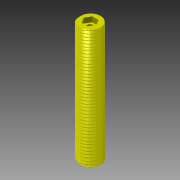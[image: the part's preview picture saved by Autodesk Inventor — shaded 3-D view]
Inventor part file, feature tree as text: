
AUTODESK INVENTOR PART (.ipt)
format: ipt  version: 2013 (Build 170138000, 138)  size: 762,880 bytes
history: native  units: mm
features: sketch x3, extrude x2, helix x1, projected_geometry x1
ambient origin geometry x8: Origin, YZ Plane, XZ Plane, XY Plane, X Axis, Y Axis, Z Axis, Center Point
bodies: Solid1 (feature_tree)
feature tree (7):
  extrude  "Extrusion1"  Depth=5.0mm
  helix  "Coil1"  [1 undecoded]
  extrude  "Extrusion2"  Depth=7.5mm
  sketch  "Sketch1"  dims[d0=14.8mm d2=5.0mm d3=82.0mm d4=0.0mm]
  sketch  "Sketch2"  dims[d5=2.0mm]
  sketch  "Sketch3"  dims[d6=2.001mm d7=10.0mm d8=500.0mm d9=0.0mm d10=90.0deg d11=90.0deg d12=0.0mm d13=0.0mm d14=7.5mm d15=3.5mm d16=0.0mm]
  projected_geometry  "Project Cut Edges1"
note: 1 required parameter value undecoded (feature->parameter linkage not recoverable at this tier; creation-order binding heuristic only, values carry confidence <= 0.55)
